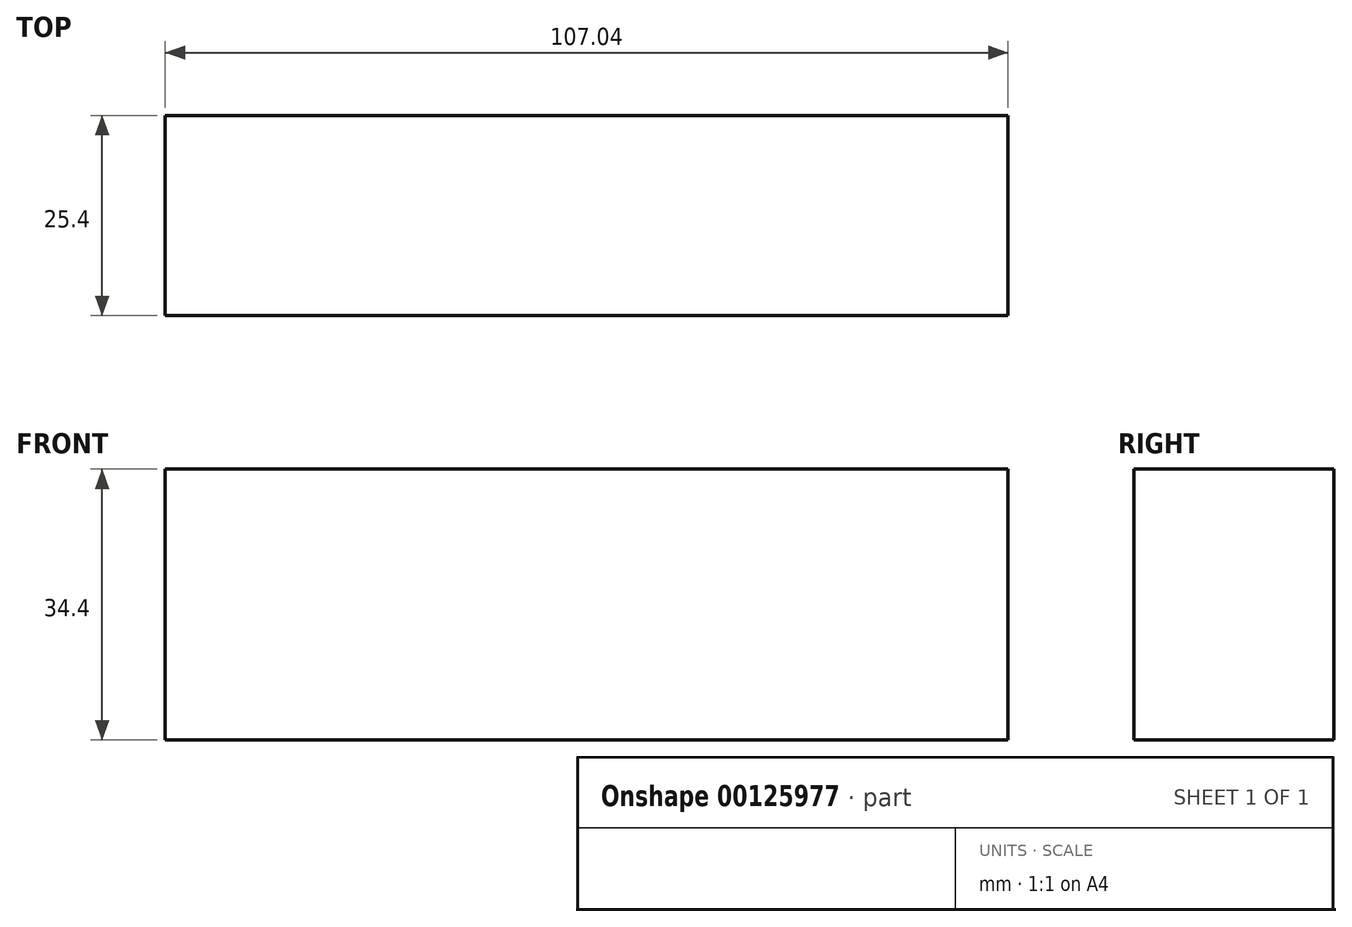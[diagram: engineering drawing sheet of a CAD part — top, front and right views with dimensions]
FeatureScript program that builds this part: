
annotation { "Feature Type Name" : "Feature", "Feature Type Description" : "" }
export const myFeature = defineFeature(function(context is Context, id is Id, definition is map)
    precondition{}
    {
        {
            var Q0;
            Q0=qCreatedBy(makeId("Front.planeOp"),FACE);
            var sketch = newSketch(context, id + "F0", { "sketchPlane" : qUnion([Q0])});
            skLineSegment(sketch, "E0.bottom", {"start": v(-53.52, -17.2) * mm, "end": v(53.52, -17.2) * mm});
            skLineSegment(sketch, "E0.top", {"start": v(-53.52, 17.2) * mm, "end": v(53.52, 17.2) * mm});
            skLineSegment(sketch, "E0.left", {"start": v(-53.52, -17.2) * mm, "end": v(-53.52, 17.2) * mm});
            skLineSegment(sketch, "E0.right", {"start": v(53.52, -17.2) * mm, "end": v(53.52, 17.2) * mm});
            skPoint(sketch, "E0.middle", {"position": v(0, 0) * mm});
            skSolve(sketch);
        }
        {
            var Q0;
            Q0=makeQuery(id+"F0.imprint","IMPRINT",FACE,{"disambiguationData":[TD([[makeQuery(id+"F0.imprint","IMPRINT",EDGE,{"derivedFrom":sQuery(id+"F0.wireOp",EDGE,"E0.bottom")}),1.0]])]});
            extrude(context, id + "F1", {"entities" : qUnion([Q0]), "depth" : 25.4 * mm});
        }
    });
